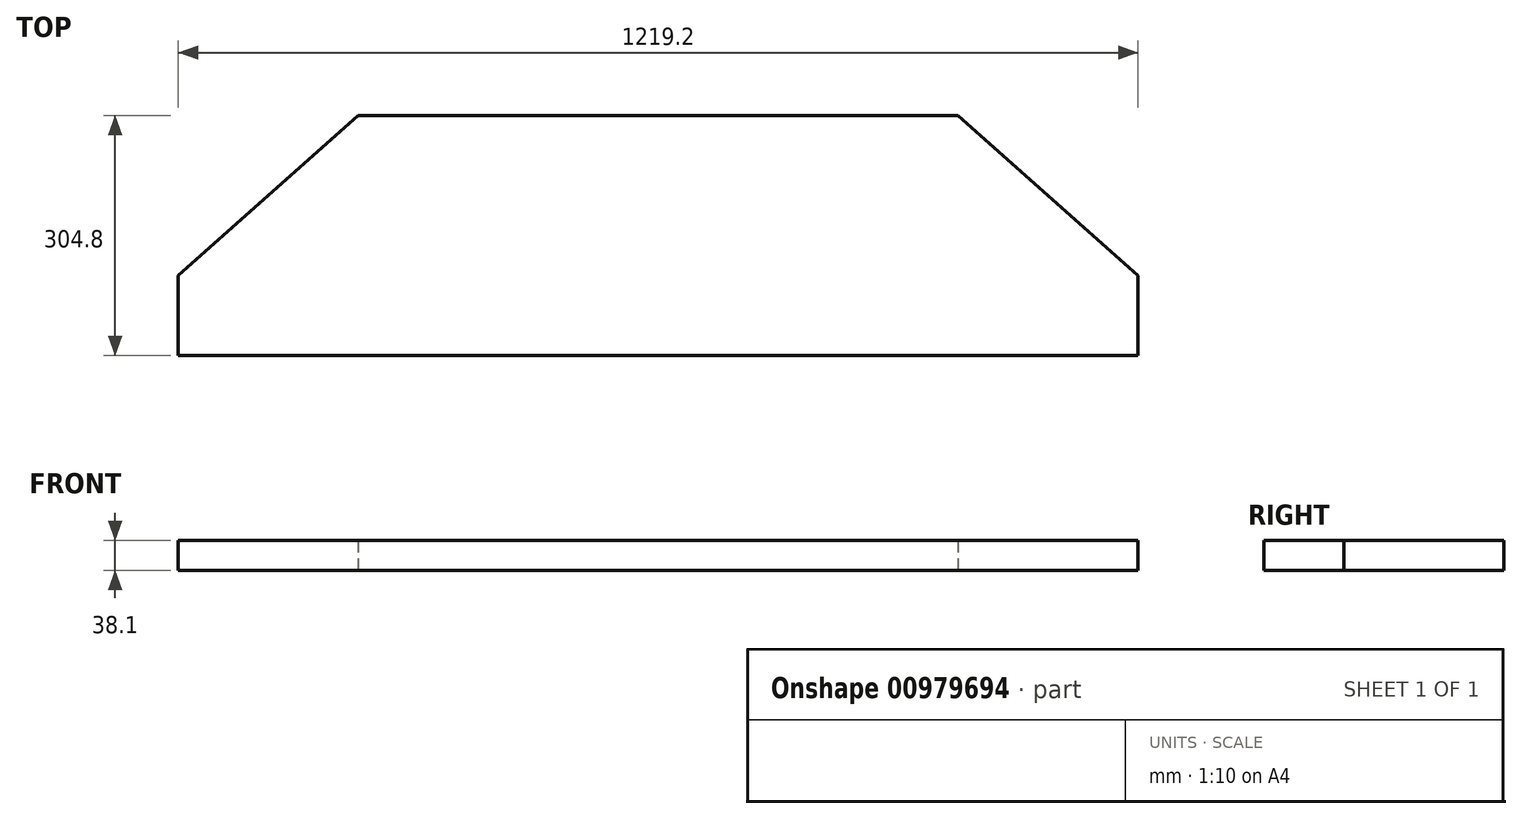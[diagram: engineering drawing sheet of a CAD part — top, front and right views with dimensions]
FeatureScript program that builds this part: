
annotation { "Feature Type Name" : "Feature", "Feature Type Description" : "" }
export const myFeature = defineFeature(function(context is Context, id is Id, definition is map)
    precondition{}
    {
        {
            var Q0;
            Q0=qCreatedBy(makeId("Top.planeOp"),FACE);
            var sketch = newSketch(context, id + "F0", { "sketchPlane" : qUnion([Q0])});
            skLineSegment(sketch, "E0.bottom", {"start": v(0, 0) * mm, "end": v(1219.2, 0) * mm});
            skLineSegment(sketch, "E0.top", {"start": v(228.6, 304.8) * mm, "end": v(990.6, 304.8) * mm});
            skLineSegment(sketch, "E0.left", {"start": v(0, 0) * mm, "end": v(0, 101.6) * mm});
            skLineSegment(sketch, "E0.right", {"start": v(1219.2, 0) * mm, "end": v(1219.2, 101.6) * mm});
            skLineSegment(sketch, "E1", {"start": v(1219.2, 101.6) * mm, "end": v(990.6, 304.8) * mm});
            skLineSegment(sketch, "E2", {"start": v(228.6, 304.8) * mm, "end": v(0, 101.6) * mm});
            skSolve(sketch);
        }
        {
            var Q0;
            Q0 = qSketchRegion(id + "F0", true);
            extrude(context, id + "F1", {"entities" : qUnion([Q0]), "depth" : 38.1 * mm, "offsetDistance" : 25.4 * mm});
        }
    });
